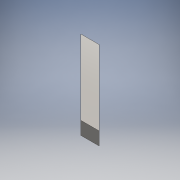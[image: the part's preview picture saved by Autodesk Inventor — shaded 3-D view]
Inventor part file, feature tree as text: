
AUTODESK INVENTOR PART (.ipt)
format: ipt  version: 2016 (Build 200138000, 138)  size: 90,624 bytes
history: native  units: mm
features: extrude x1, sketch x1
ambient origin geometry x8: Origin, YZ Plane, XZ Plane, XY Plane, X Axis, Y Axis, Z Axis, Center Point
bodies: Solid1 (feature_tree)
feature tree (2):
  extrude  "Extrusion1"  TaperAngle=45.0deg  [1 undecoded]
  sketch  "Sketch1"  dims[d0=800.0mm d1=45.0deg d3=140.0mm d4=140.0mm d5=0.0mm]
note: 1 required parameter value undecoded (feature->parameter linkage not recoverable at this tier; creation-order binding heuristic only, values carry confidence <= 0.55)
